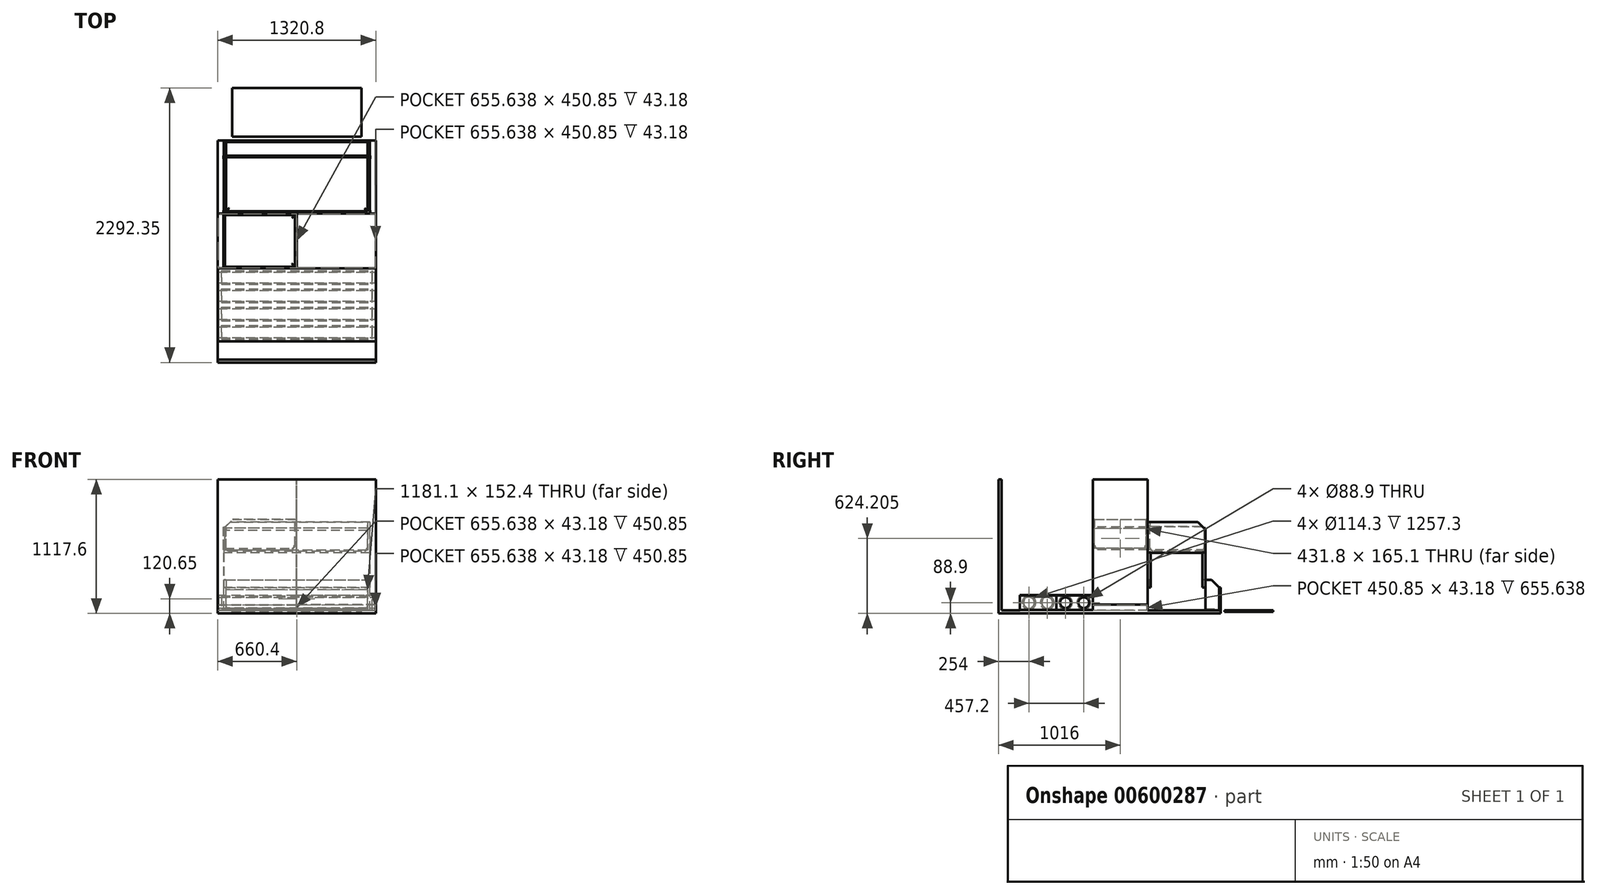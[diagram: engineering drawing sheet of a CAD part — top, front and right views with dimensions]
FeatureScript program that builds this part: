
annotation { "Feature Type Name" : "Feature", "Feature Type Description" : "" }
export const myFeature = defineFeature(function(context is Context, id is Id, definition is map)
    precondition{}
    {
        {
            var Q0;
            Q0=qCreatedBy(makeId("Top.planeOp"),FACE);
            var sketch = newSketch(context, id + "F0", { "sketchPlane" : qUnion([Q0])});
            skLineSegment(sketch, "E0.bottom", {"start": v(660.4, 914.4) * mm, "end": v(-660.4, 914.4) * mm});
            skLineSegment(sketch, "E0.top", {"start": v(660.4, -914.4) * mm, "end": v(-660.4, -914.4) * mm});
            skLineSegment(sketch, "E0.left", {"start": v(660.4, 914.4) * mm, "end": v(660.4, -914.4) * mm});
            skLineSegment(sketch, "E0.right", {"start": v(-660.4, 914.4) * mm, "end": v(-660.4, -914.4) * mm});
            skPoint(sketch, "E0.middle", {"position": v(0, 0) * mm});
            skSolve(sketch);
        }
        {
            var Q0;
            Q0 = qSketchRegion(id + "F0", true);
            extrude(context, id + "F1", {"entities" : qUnion([Q0]), "oppositeDirection" : true, "depth" : 25.4 * mm, "offsetDistance" : 25.4 * mm});
        }
        {
            var Q0;
            Q0=makeQuery(id+"F1.opExtrude","SWEPT_FACE",FACE,{"disambiguationData":[OSD([sQuery(id+"F0.wireOp",EDGE,"E0.top")])]});
            var sketch = newSketch(context, id + "F2", { "sketchPlane" : qUnion([Q0])});
            skLineSegment(sketch, "E1.bottom", {"start": v(-660.4, -25.4) * mm, "end": v(660.4, -25.4) * mm});
            skLineSegment(sketch, "E1.top", {"start": v(-660.4, 1092.2) * mm, "end": v(660.4, 1092.2) * mm});
            skLineSegment(sketch, "E1.left", {"start": v(-660.4, -25.4) * mm, "end": v(-660.4, 1092.2) * mm});
            skLineSegment(sketch, "E1.right", {"start": v(660.4, -25.4) * mm, "end": v(660.4, 1092.2) * mm});
            skSolve(sketch);
        }
        {
            var Q0;
            Q0 = qSketchRegion(id + "F2", true);
            extrude(context, id + "F3", {"entities" : qUnion([Q0]), "operationType" : NewBodyOperationType.ADD, "depth" : 25.4 * mm, "offsetDistance" : 25.4 * mm});
        }
        {
            var Q0;
            Q0=makeQuery(id+"F1.opExtrude","CAP_FACE",FACE,{"disambiguationData":[OSD([sQuery(id+"F0.wireOp",EDGE,"E0.bottom"),sQuery(id+"F0.wireOp",EDGE,"E0.top"),sQuery(id+"F0.wireOp",EDGE,"E0.left"),sQuery(id+"F0.wireOp",EDGE,"E0.right")])],"isStart":true});
            var sketch = newSketch(context, id + "F4", { "sketchPlane" : qUnion([Q0])});
            skLineSegment(sketch, "E2.bottom", {"start": v(-609.6, 914.4) * mm, "end": v(609.6, 914.4) * mm});
            skLineSegment(sketch, "E2.top", {"start": v(-609.6, 304.8) * mm, "end": v(609.6, 304.8) * mm});
            skLineSegment(sketch, "E2.left", {"start": v(-609.6, 914.4) * mm, "end": v(-609.6, 304.8) * mm});
            skLineSegment(sketch, "E2.right", {"start": v(609.6, 914.4) * mm, "end": v(609.6, 304.8) * mm});
            skLineSegment(sketch, "E3", {"start": v(0, 914.4) * mm, "end": v(0, 798.92) * mm, "construction": true});
            skPoint(sketch, "E3.endSnap0", {"position": v(0, 914.4) * mm});
            skPoint(sketch, "E4.visualSharp", {"position": v(-609.6, 914.4) * mm});
            skLineSegment(sketch, "E4.filletArc", {"start": v(-609.6, 914.4) * mm, "end": v(-609.6, 914.4) * mm});
            skPoint(sketch, "E5.visualSharp", {"position": v(-609.6, 304.8) * mm});
            skLineSegment(sketch, "E5.filletArc", {"start": v(-609.6, 304.8) * mm, "end": v(-609.6, 304.8) * mm});
            skPoint(sketch, "E6.visualSharp", {"position": v(609.6, 304.8) * mm});
            skLineSegment(sketch, "E6.filletArc", {"start": v(609.6, 304.8) * mm, "end": v(609.6, 304.8) * mm});
            skPoint(sketch, "E7.visualSharp", {"position": v(609.6, 914.4) * mm});
            skLineSegment(sketch, "E7.filletArc", {"start": v(609.6, 914.4) * mm, "end": v(609.6, 914.4) * mm});
            skSolve(sketch);
        }
        {
            var Q0;
            Q0 = qSketchRegion(id + "F4", true);
            extrude(context, id + "F5", {"entities" : qUnion([Q0]), "depth" : 254 * mm, "offsetDistance" : 25.4 * mm});
        }
        {
            var Q0;
            Q0=makeQuery(id+"F5.opExtrude","CAP_FACE",FACE,{"disambiguationData":[OSD([sQuery(id+"F4.wireOp",EDGE,"E2.bottom"),sQuery(id+"F4.wireOp",EDGE,"E2.top"),sQuery(id+"F4.wireOp",EDGE,"E2.left"),sQuery(id+"F4.wireOp",EDGE,"E2.right"),sQuery(id+"F4.wireOp",EDGE,"E4.filletArc"),sQuery(id+"F4.wireOp",EDGE,"E5.filletArc"),sQuery(id+"F4.wireOp",EDGE,"E6.filletArc"),sQuery(id+"F4.wireOp",EDGE,"E7.filletArc")])],"isStart":false});
            var sketch = newSketch(context, id + "F6", { "sketchPlane" : qUnion([Q0])});
            skLineSegment(sketch, "E8.0", {"start": v(590.55, 330.2) * mm, "end": v(590.55, 889) * mm});
            skLineSegment(sketch, "E8.1", {"start": v(-584.2, 323.85) * mm, "end": v(584.2, 323.85) * mm});
            skLineSegment(sketch, "E8.2", {"start": v(-590.55, 889) * mm, "end": v(-590.55, 330.2) * mm});
            skLineSegment(sketch, "E8.3", {"start": v(584.2, 895.35) * mm, "end": v(-584.2, 895.35) * mm});
            skPoint(sketch, "E9.visualSharp", {"position": v(-590.55, 895.35) * mm});
            skArc(sketch, "E9.filletArc", {"start": v(-584.2, 895.35) * mm, "mid": v(-588.7, 893.5) * mm, "end": v(-590.55, 889) * mm});
            skPoint(sketch, "E10.visualSharp", {"position": v(-590.55, 323.85) * mm});
            skArc(sketch, "E10.filletArc", {"start": v(-590.55, 330.2) * mm, "mid": v(-588.7, 325.7) * mm, "end": v(-584.2, 323.85) * mm});
            skPoint(sketch, "E11.visualSharp", {"position": v(590.55, 323.85) * mm});
            skArc(sketch, "E11.filletArc", {"start": v(584.2, 323.85) * mm, "mid": v(588.7, 325.7) * mm, "end": v(590.55, 330.2) * mm});
            skPoint(sketch, "E12.visualSharp", {"position": v(590.55, 895.35) * mm});
            skArc(sketch, "E12.filletArc", {"start": v(590.55, 889) * mm, "mid": v(588.7, 893.5) * mm, "end": v(584.2, 895.35) * mm});
            skLineSegment(sketch, "E13.bottom", {"start": v(-6.35, 895.35) * mm, "end": v(6.35, 895.35) * mm});
            skLineSegment(sketch, "E13.top", {"start": v(-6.35, 323.85) * mm, "end": v(6.35, 323.85) * mm});
            skLineSegment(sketch, "E13.left", {"start": v(-6.35, 895.35) * mm, "end": v(-6.35, 323.85) * mm, "construction": true});
            skLineSegment(sketch, "E13.right", {"start": v(6.35, 895.35) * mm, "end": v(6.35, 323.85) * mm, "construction": true});
            skLineSegment(sketch, "E14", {"start": v(0, 895.35) * mm, "end": v(0, 323.85) * mm, "construction": true});
            skSolve(sketch);
        }
        {
            var Q0;
            Q0=makeQuery(id+"F6.imprint","IMPRINT",FACE,{"disambiguationData":[TD([[makeQuery(id+"F6.imprint","IMPRINT",EDGE,{"derivedFrom":sQuery(id+"F6.wireOp",EDGE,"E8.0")}),1.0]])]});
            var Q1;
            Q1=makeQuery(id+"F6.imprint","IMPRINT",FACE,{"disambiguationData":[TD([[makeQuery(id+"F6.imprint","IMPRINT",EDGE,{"derivedFrom":sQuery(id+"F6.wireOp",EDGE,"E8.2")}),1.0]])]});
            extrude(context, id + "F7", {"entities" : qUnion([Q0, Q1]), "operationType" : NewBodyOperationType.REMOVE, "oppositeDirection" : true, "depth" : 241.3 * mm, "offsetDistance" : 25.4 * mm});
        }
        {
            var Q0;
            Q0=makeQuery(id+"F7.boolean.opBoolean","COPY",FACE,{"derivedFrom":makeQuery(id+"F7.opExtrude","CAP_FACE",FACE,{"disambiguationData":[OSD([sQuery(id+"F6.wireOp",EDGE,"E8.0"),sQuery(id+"F6.wireOp",EDGE,"E8.1"),sQuery(id+"F6.wireOp",EDGE,"E8.3"),sQuery(id+"F6.wireOp",EDGE,"E11.filletArc"),sQuery(id+"F6.wireOp",EDGE,"E12.filletArc"),sQuery(id+"F6.wireOp",EDGE,"E13.right")])],"isStart":false})});
            var Q1;
            Q1=makeQuery(id+"F7.boolean.opBoolean","COPY",FACE,{"derivedFrom":makeQuery(id+"F7.opExtrude","CAP_FACE",FACE,{"disambiguationData":[OSD([sQuery(id+"F6.wireOp",EDGE,"E8.1"),sQuery(id+"F6.wireOp",EDGE,"E8.2"),sQuery(id+"F6.wireOp",EDGE,"E8.3"),sQuery(id+"F6.wireOp",EDGE,"E9.filletArc"),sQuery(id+"F6.wireOp",EDGE,"E10.filletArc"),sQuery(id+"F6.wireOp",EDGE,"E13.left")])],"isStart":false})});
            fillet(context, id + "F8", {"entities" : qUnion([Q0, Q1]), "radius" : 25.4 * mm, "tangentPropagation" : true, "allowEdgeOverflow" : false});
        }
        {
            var Q0;
            Q0=makeQuery(id+"F1.opExtrude","SWEPT_FACE",FACE,{"disambiguationData":[OSD([sQuery(id+"F0.wireOp",EDGE,"E0.bottom")])]});
            cPlane(context, id + "F9", {"entities" : qUnion([Q0]), "cplaneType" : CPlaneType.OFFSET, "offset" : 127 * mm, "oppositeDirection" : true, "width" : 152.4 * mm, "height" : 152.4 * mm});
        }
        {
            var Q0;
            Q0=qCreatedBy(id+"F9.planeOp",FACE);
            var sketch = newSketch(context, id + "F10", { "sketchPlane" : qUnion([Q0])});
            skLineSegment(sketch, "E15.0", {"start": v(-660.4, 0) * mm, "end": v(660.4, 0) * mm});
            skLineSegment(sketch, "E16.bottom", {"start": v(-612.78, 0) * mm, "end": v(-609.6, 0) * mm});
            skLineSegment(sketch, "E16.top", {"start": v(-612.77, 482.6) * mm, "end": v(-609.6, 482.6) * mm});
            skLineSegment(sketch, "E16.left", {"start": v(-612.78, 0) * mm, "end": v(-612.77, 482.6) * mm});
            skLineSegment(sketch, "E16.right", {"start": v(-609.6, 0) * mm, "end": v(-609.6, 482.6) * mm});
            skLineSegment(sketch, "E17.bottom", {"start": v(-612.77, 482.6) * mm, "end": v(612.77, 482.6) * mm});
            skLineSegment(sketch, "E17.top", {"start": v(-612.77, 479.43) * mm, "end": v(612.77, 479.43) * mm});
            skLineSegment(sketch, "E17.left", {"start": v(-612.77, 482.6) * mm, "end": v(-612.77, 479.43) * mm});
            skLineSegment(sketch, "E17.right", {"start": v(612.78, 482.6) * mm, "end": v(612.78, 479.43) * mm});
            skLineSegment(sketch, "E18.bottom", {"start": v(612.77, 482.6) * mm, "end": v(609.6, 482.6) * mm});
            skLineSegment(sketch, "E18.top", {"start": v(612.78, 0) * mm, "end": v(609.6, 0) * mm});
            skLineSegment(sketch, "E18.left", {"start": v(612.78, 482.6) * mm, "end": v(612.77, 0) * mm});
            skLineSegment(sketch, "E18.right", {"start": v(609.6, 482.6) * mm, "end": v(609.6, 0) * mm});
            skLineSegment(sketch, "E19", {"start": v(0, 0) * mm, "end": v(0, 100.43) * mm, "construction": true});
            skLineSegment(sketch, "E20.bottom", {"start": v(-612.78, 0) * mm, "end": v(-600.08, 0) * mm});
            skLineSegment(sketch, "E20.top", {"start": v(-612.78, 3.18) * mm, "end": v(-600.08, 3.18) * mm});
            skLineSegment(sketch, "E20.left", {"start": v(-612.78, 0) * mm, "end": v(-612.78, 3.18) * mm});
            skLineSegment(sketch, "E20.right", {"start": v(-600.08, 0) * mm, "end": v(-600.08, 3.18) * mm});
            skLineSegment(sketch, "E21.MirrorCS", {"start": v(612.78, 3.18) * mm, "end": v(600.08, 3.18) * mm});
            skLineSegment(sketch, "E22.MirrorCS", {"start": v(600.08, 0) * mm, "end": v(600.08, 3.18) * mm});
            skSolve(sketch);
        }
        {
            var Q0;
            {var subQ0=sQuery(id+"F10.wireOp",EDGE,"E16.bottom");Q0=makeQuery(id+"F10.imprint","IMPRINT",FACE,{"disambiguationData":[TD([[makeQuery(id+"F10.imprint","IMPRINT",EDGE,{"derivedFrom":subQ0}),1.0]])]});}
            var Q1;
            {var subQ5=sQuery(id+"F10.wireOp",EDGE,"E17.left");Q1=makeQuery(id+"F10.imprint","IMPRINT",FACE,{"disambiguationData":[TD([[makeQuery(id+"F10.imprint","IMPRINT",EDGE,{"derivedFrom":subQ5}),1.0]])]});}
            var Q2;
            {var subQ5=sQuery(id+"F10.wireOp",EDGE,"E18.bottom");Q2=makeQuery(id+"F10.imprint","IMPRINT",FACE,{"disambiguationData":[TD([[makeQuery(id+"F10.imprint","IMPRINT",EDGE,{"derivedFrom":subQ5}),1.0]])]});}
            var Q3;
            {var subQ5=sQuery(id+"F10.wireOp",EDGE,"E18.top");Q3=makeQuery(id+"F10.imprint","IMPRINT",FACE,{"disambiguationData":[TD([[makeQuery(id+"F10.imprint","IMPRINT",EDGE,{"derivedFrom":subQ5}),-1.0]])]});}
            var Q4;
            {var subQ0=sQuery(id+"F10.wireOp",EDGE,"E17.bottom");var subQ1=sQuery(id+"F10.wireOp",EDGE,"E16.right");var subQ2=makeQuery(id+"F10.imprint","INTERSECT",VERTEX,{"derivedFrom":[subQ1,subQ0]});Q4=makeQuery(id+"F10.imprint","IMPRINT",FACE,{"disambiguationData":[TD([[makeQuery(id+"F10.imprint","IMPRINT",EDGE,{"disambiguationData":[TD([[subQ2,1.0]])],"derivedFrom":subQ1}),-1.0]])]});}
            var Q5;
            {var subQ3=sQuery(id+"F10.wireOp",EDGE,"E22.MirrorCS");Q5=makeQuery(id+"F10.imprint","IMPRINT",FACE,{"disambiguationData":[TD([[makeQuery(id+"F10.imprint","IMPRINT",EDGE,{"derivedFrom":subQ3}),-1.0]])]});}
            var Q6;
            {var subQ0=sQuery(id+"F10.wireOp",EDGE,"E18.left");var subQ1=sQuery(id+"F10.wireOp",EDGE,"E17.top");var subQ2=makeQuery(id+"F10.imprint","INTERSECT",VERTEX,{"derivedFrom":[subQ1,subQ0]});Q6=makeQuery(id+"F10.imprint","IMPRINT",FACE,{"disambiguationData":[TD([[makeQuery(id+"F10.imprint","IMPRINT",EDGE,{"disambiguationData":[TD([[subQ2,1.0]])],"derivedFrom":subQ1}),-1.0]])]});}
            var Q7;
            {var subQ5=sQuery(id+"F10.wireOp",EDGE,"E20.right");Q7=makeQuery(id+"F10.imprint","IMPRINT",FACE,{"disambiguationData":[TD([[makeQuery(id+"F10.imprint","IMPRINT",EDGE,{"derivedFrom":subQ5}),1.0]])]});}
            var Q8;
            {var subQ5=sQuery(id+"F10.wireOp",EDGE,"E20.left");Q8=makeQuery(id+"F10.imprint","IMPRINT",FACE,{"disambiguationData":[TD([[makeQuery(id+"F10.imprint","IMPRINT",EDGE,{"derivedFrom":subQ5}),-1.0]])]});}
            var Q9;
            {var subQ0=sQuery(id+"F10.wireOp",EDGE,"E16.left");Q9=makeQuery(id+"F10.imprint","IMPRINT",FACE,{"disambiguationData":[TD([[makeQuery(id+"F10.imprint","IMPRINT",EDGE,{"derivedFrom":subQ0}),-1.0]])]});}
            extrude(context, id + "F11", {"entities" : qUnion([Q0, Q1, Q2, Q3, Q4, Q5, Q6, Q7, Q8, Q9]), "oppositeDirection" : true, "depth" : 482.6 * mm, "offsetDistance" : 25.4 * mm});
        }
        {
            var Q0;
            Q0=makeQuery(id+"F5.opExtrude","SWEPT_FACE",FACE,{"disambiguationData":[OSD([sQuery(id+"F4.wireOp",EDGE,"E2.right")])]});
            var sketch = newSketch(context, id + "F12", { "sketchPlane" : qUnion([Q0])});
            skLineSegment(sketch, "E23", {"start": v(838.2, 254) * mm, "end": v(914.4, 177.8) * mm});
            skLineSegment(sketch, "E24.0", {"start": v(914.4, 254) * mm, "end": v(914.4, 0) * mm, "construction": true});
            skLineSegment(sketch, "E25.bottom", {"start": v(901.7, 0) * mm, "end": v(980.54, 0) * mm});
            skLineSegment(sketch, "E25.top", {"start": v(901.7, 254) * mm, "end": v(980.54, 254) * mm});
            skLineSegment(sketch, "E25.left", {"start": v(901.7, 0) * mm, "end": v(901.7, 190.5) * mm});
            skLineSegment(sketch, "E25.right", {"start": v(980.54, 0) * mm, "end": v(980.54, 254) * mm});
            skSolve(sketch);
        }
        {
            var Q0;
            Q0 = qSketchRegion(id + "F12", true);
            var Q1;
            {var subQ0=sQuery(id+"F12.wireOp",EDGE,"E23");var subQ1=sQuery(id+"F4.wireOp",EDGE,"E2.right");var subQ2=makeQuery(id+"F5.opExtrude","CAP_EDGE",EDGE,{"disambiguationData":[OSD([subQ1])],"isStart":false});var subQ3=makeQuery(id+"F12.imprint","INTERSECT",VERTEX,{"derivedFrom":[subQ2,subQ0]});Q1=makeQuery(id+"F12.imprint","IMPRINT",FACE,{"disambiguationData":[TD([[makeQuery(id+"F12.imprint","IMPRINT",EDGE,{"disambiguationData":[TD([[subQ3,-1.0]])],"derivedFrom":subQ0}),1.0]])]});}
            var Q2;
            {var subQ0=sQuery(id+"F12.wireOp",EDGE,"E25.left");Q2=makeQuery(id+"F12.imprint","IMPRINT",FACE,{"disambiguationData":[TD([[makeQuery(id+"F12.imprint","IMPRINT",EDGE,{"derivedFrom":subQ0}),-1.0]])]});}
            var Q3;
            {var subQ0=sQuery(id+"F12.wireOp",EDGE,"E25.right");Q3=makeQuery(id+"F12.imprint","IMPRINT",FACE,{"disambiguationData":[TD([[makeQuery(id+"F12.imprint","IMPRINT",EDGE,{"derivedFrom":subQ0}),1.0]])]});}
            extrude(context, id + "F13", {"entities" : qUnion([Q0, Q1, Q2, Q3]), "operationType" : NewBodyOperationType.REMOVE, "endBound" : BoundingType.THROUGH_ALL, "oppositeDirection" : true, "depth" : 25.4 * mm, "offsetDistance" : 25.4 * mm});
        }
        {
            var Q0;
            Q0=makeQuery(id+"F13.boolean.opBoolean","COPY",FACE,{"derivedFrom":makeQuery(id+"F13.opExtrude","SWEPT_FACE",FACE,{"disambiguationData":[OSD([sQuery(id+"F12.wireOp",EDGE,"E25.left")])]})});
            var sketch = newSketch(context, id + "F14", { "sketchPlane" : qUnion([Q0])});
            skArc(sketch, "E26.0.0", {"start": v(-565.15, 12.7) * mm, "mid": v(-583.11, 20.14) * mm, "end": v(-590.55, 38.1) * mm});
            skArc(sketch, "E26.0.2", {"start": v(-590.55, 38.1) * mm, "mid": v(-583.11, 20.14) * mm, "end": v(-565.15, 12.7) * mm});
            skLineSegment(sketch, "E27.0.0", {"start": v(565.15, 12.7) * mm, "end": v(-565.15, 12.7) * mm});
            skLineSegment(sketch, "E27.0.2", {"start": v(-565.15, 12.7) * mm, "end": v(565.15, 12.7) * mm});
            skArc(sketch, "E28.0.0", {"start": v(590.55, 38.1) * mm, "mid": v(583.11, 20.14) * mm, "end": v(565.15, 12.7) * mm});
            skArc(sketch, "E28.0.2", {"start": v(590.55, 38.1) * mm, "mid": v(583.11, 20.14) * mm, "end": v(565.15, 12.7) * mm});
            skLineSegment(sketch, "E29.0", {"start": v(-590.55, 38.1) * mm, "end": v(-590.55, 203.2) * mm});
            skLineSegment(sketch, "E30.0", {"start": v(590.55, 38.1) * mm, "end": v(590.55, 203.2) * mm});
            skLineSegment(sketch, "E31", {"start": v(590.55, 203.2) * mm, "end": v(-590.55, 203.2) * mm});
            skSolve(sketch);
        }
        {
            var Q0;
            Q0 = qSketchRegion(id + "F14", true);
            extrude(context, id + "F15", {"entities" : qUnion([Q0]), "operationType" : NewBodyOperationType.REMOVE, "oppositeDirection" : true, "depth" : 50.8 * mm, "offsetDistance" : 25.4 * mm});
        }
        {
            var Q0;
            Q0=makeQuery(id+"F13.boolean.opBoolean","COPY",FACE,{"derivedFrom":makeQuery(id+"F13.opExtrude","SWEPT_FACE",FACE,{"disambiguationData":[OSD([sQuery(id+"F12.wireOp",EDGE,"E25.left")])]})});
            var sketch = newSketch(context, id + "F16", { "sketchPlane" : qUnion([Q0])});
            skLineSegment(sketch, "E32.bottom", {"start": v(-609.6, 190.5) * mm, "end": v(609.6, 190.5) * mm});
            skLineSegment(sketch, "E32.top", {"start": v(-609.6, 0) * mm, "end": v(609.6, 0) * mm});
            skLineSegment(sketch, "E32.left", {"start": v(-609.6, 190.5) * mm, "end": v(-609.6, 0) * mm});
            skLineSegment(sketch, "E32.right", {"start": v(609.6, 190.5) * mm, "end": v(609.6, 0) * mm});
            skLineSegment(sketch, "E33.0", {"start": v(-590.55, 171.45) * mm, "end": v(590.55, 171.45) * mm});
            skLineSegment(sketch, "E33.1", {"start": v(-590.55, 171.45) * mm, "end": v(-590.55, 19.05) * mm});
            skLineSegment(sketch, "E33.2", {"start": v(-590.55, 19.05) * mm, "end": v(590.55, 19.05) * mm});
            skLineSegment(sketch, "E33.3", {"start": v(590.55, 171.45) * mm, "end": v(590.55, 19.05) * mm});
            skSolve(sketch);
        }
        {
            var Q0;
            Q0 = qSketchRegion(id + "F16", true);
            extrude(context, id + "F17", {"entities" : qUnion([Q0]), "depth" : 12.7 * mm, "offsetDistance" : 25.4 * mm});
        }
        {
            var Q0;
            Q0=makeQuery(id+"F17.opExtrude","CAP_FACE",FACE,{"disambiguationData":[OSD([sQuery(id+"F16.wireOp",EDGE,"E32.bottom"),sQuery(id+"F16.wireOp",EDGE,"E32.top"),sQuery(id+"F16.wireOp",EDGE,"E32.left"),sQuery(id+"F16.wireOp",EDGE,"E32.right"),sQuery(id+"F16.wireOp",EDGE,"E33.0"),sQuery(id+"F16.wireOp",EDGE,"E33.1"),sQuery(id+"F16.wireOp",EDGE,"E33.2"),sQuery(id+"F16.wireOp",EDGE,"E33.3")])],"isStart":false});
            var sketch = newSketch(context, id + "F18", { "sketchPlane" : qUnion([Q0])});
            skLineSegment(sketch, "E34.0", {"start": v(-590.55, 171.45) * mm, "end": v(590.55, 171.45) * mm});
            skLineSegment(sketch, "E34.1", {"start": v(-590.55, 171.45) * mm, "end": v(-590.55, 19.05) * mm});
            skLineSegment(sketch, "E34.2", {"start": v(-590.55, 19.05) * mm, "end": v(590.55, 19.05) * mm});
            skLineSegment(sketch, "E34.3", {"start": v(590.55, 19.05) * mm, "end": v(590.55, 171.45) * mm});
            skSolve(sketch);
        }
        {
            var Q0;
            Q0 = qSketchRegion(id + "F18", true);
            extrude(context, id + "F19", {"entities" : qUnion([Q0]), "oppositeDirection" : true, "depth" : 12.7 * mm, "offsetDistance" : 25.4 * mm});
        }
        {
            var Q0;
            Q0=makeQuery(id+"F11.opExtrude","SWEPT_FACE",FACE,{"disambiguationData":[OSD([sQuery(id+"F10.wireOp",EDGE,"E17.bottom"),sQuery(id+"F10.wireOp",EDGE,"E18.bottom")])]});
            var sketch = newSketch(context, id + "F20", { "sketchPlane" : qUnion([Q0])});
            skLineSegment(sketch, "E35.bottom", {"start": v(-609.6, 304.8) * mm, "end": v(609.6, 304.8) * mm});
            skLineSegment(sketch, "E35.top", {"start": v(-609.6, 787.4) * mm, "end": v(609.6, 787.4) * mm});
            skLineSegment(sketch, "E35.left", {"start": v(-609.6, 304.8) * mm, "end": v(-609.6, 787.4) * mm});
            skLineSegment(sketch, "E35.right", {"start": v(609.6, 304.8) * mm, "end": v(609.6, 787.4) * mm});
            skLineSegment(sketch, "E36", {"start": v(0, 0) * mm, "end": v(0, 135.1) * mm, "construction": true});
            skSolve(sketch);
        }
        {
            var Q0;
            Q0 = qSketchRegion(id + "F20", true);
            extrude(context, id + "F21", {"entities" : qUnion([Q0]), "depth" : 254 * mm, "offsetDistance" : 25.4 * mm});
        }
        {
            var Q0;
            Q0=makeQuery(id+"F21.opExtrude","CAP_FACE",FACE,{"disambiguationData":[OSD([sQuery(id+"F20.wireOp",EDGE,"E35.bottom"),sQuery(id+"F20.wireOp",EDGE,"E35.top"),sQuery(id+"F20.wireOp",EDGE,"E35.left"),sQuery(id+"F20.wireOp",EDGE,"E35.right")])],"isStart":false});
            var sketch = newSketch(context, id + "F22", { "sketchPlane" : qUnion([Q0])});
            skLineSegment(sketch, "E37.0", {"start": v(-584.2, 323.85) * mm, "end": v(584.2, 323.85) * mm});
            skLineSegment(sketch, "E37.1", {"start": v(-590.55, 762) * mm, "end": v(-590.55, 330.2) * mm});
            skLineSegment(sketch, "E37.2", {"start": v(584.2, 768.35) * mm, "end": v(-584.2, 768.35) * mm});
            skLineSegment(sketch, "E37.3", {"start": v(590.55, 330.2) * mm, "end": v(590.55, 762) * mm});
            skPoint(sketch, "E38.visualSharp", {"position": v(-590.55, 768.35) * mm});
            skArc(sketch, "E38.filletArc", {"start": v(-584.2, 768.35) * mm, "mid": v(-588.7, 766.5) * mm, "end": v(-590.55, 762) * mm});
            skPoint(sketch, "E39.visualSharp", {"position": v(-590.55, 323.85) * mm});
            skArc(sketch, "E39.filletArc", {"start": v(-590.55, 330.2) * mm, "mid": v(-588.7, 325.7) * mm, "end": v(-584.2, 323.85) * mm});
            skPoint(sketch, "E40.visualSharp", {"position": v(590.55, 323.85) * mm});
            skArc(sketch, "E40.filletArc", {"start": v(584.2, 323.85) * mm, "mid": v(588.7, 325.7) * mm, "end": v(590.55, 330.2) * mm});
            skPoint(sketch, "E41.visualSharp", {"position": v(590.55, 768.35) * mm});
            skArc(sketch, "E41.filletArc", {"start": v(590.55, 762) * mm, "mid": v(588.7, 766.5) * mm, "end": v(584.2, 768.35) * mm});
            skSolve(sketch);
        }
        {
            var Q0;
            Q0 = qSketchRegion(id + "F22", true);
            extrude(context, id + "F23", {"entities" : qUnion([Q0]), "operationType" : NewBodyOperationType.REMOVE, "oppositeDirection" : true, "depth" : 241.3 * mm, "offsetDistance" : 25.4 * mm});
        }
        {
            var Q0;
            Q0=makeQuery(id+"F23.boolean.opBoolean","COPY",EDGE,{"derivedFrom":makeQuery(id+"F23.opExtrude","CAP_EDGE",EDGE,{"disambiguationData":[OSD([sQuery(id+"F22.wireOp",EDGE,"E37.0")])],"isStart":false})});
            var Q1;
            Q1=makeQuery(id+"F23.boolean.opBoolean","COPY",EDGE,{"derivedFrom":makeQuery(id+"F23.opExtrude","CAP_EDGE",EDGE,{"disambiguationData":[OSD([sQuery(id+"F22.wireOp",EDGE,"E37.1")])],"isStart":false})});
            var Q2;
            Q2=makeQuery(id+"F23.boolean.opBoolean","COPY",EDGE,{"derivedFrom":makeQuery(id+"F23.opExtrude","CAP_EDGE",EDGE,{"disambiguationData":[OSD([sQuery(id+"F22.wireOp",EDGE,"E37.3")])],"isStart":false})});
            fillet(context, id + "F24", {"entities" : qUnion([Q0, Q1, Q2]), "radius" : 25.4 * mm, "tangentPropagation" : true, "allowEdgeOverflow" : false});
        }
        {
            var Q0;
            Q0=makeQuery(id+"F21.opExtrude","SWEPT_FACE",FACE,{"disambiguationData":[OSD([sQuery(id+"F20.wireOp",EDGE,"E35.right")])]});
            var sketch = newSketch(context, id + "F25", { "sketchPlane" : qUnion([Q0])});
            skLineSegment(sketch, "E42", {"start": v(723.9, 736.6) * mm, "end": v(774.7, 685.8) * mm});
            skLineSegment(sketch, "E43.bottom", {"start": v(787.4, 482.6) * mm, "end": v(774.7, 482.6) * mm});
            skLineSegment(sketch, "E43.top", {"start": v(787.4, 736.6) * mm, "end": v(774.7, 736.6) * mm});
            skLineSegment(sketch, "E43.left", {"start": v(787.4, 482.6) * mm, "end": v(787.4, 736.6) * mm});
            skLineSegment(sketch, "E43.right", {"start": v(774.7, 482.6) * mm, "end": v(774.7, 685.8) * mm});
            skLineSegment(sketch, "E44", {"start": v(723.9, 736.6) * mm, "end": v(787.4, 736.6) * mm});
            skPoint(sketch, "E45.orphan", {"position": v(787.4, 673.1) * mm});
            skSolve(sketch);
        }
        {
            var Q0;
            Q0 = qSketchRegion(id + "F25", true);
            extrude(context, id + "F26", {"entities" : qUnion([Q0]), "operationType" : NewBodyOperationType.REMOVE, "endBound" : BoundingType.THROUGH_ALL, "oppositeDirection" : true, "depth" : 25.4 * mm, "offsetDistance" : 25.4 * mm});
        }
        {
            var Q0;
            Q0=makeQuery(id+"F26.boolean.opBoolean","COPY",FACE,{"derivedFrom":makeQuery(id+"F26.opExtrude","SWEPT_FACE",FACE,{"disambiguationData":[OSD([sQuery(id+"F25.wireOp",EDGE,"E43.right")])]})});
            var sketch = newSketch(context, id + "F27", { "sketchPlane" : qUnion([Q0])});
            skArc(sketch, "E46.0.0", {"start": v(-565.15, 495.3) * mm, "mid": v(-583.11, 502.74) * mm, "end": v(-590.55, 520.7) * mm});
            skArc(sketch, "E46.0.2", {"start": v(-590.55, 520.7) * mm, "mid": v(-583.11, 502.74) * mm, "end": v(-565.15, 495.3) * mm});
            skLineSegment(sketch, "E47.0", {"start": v(-590.55, 520.7) * mm, "end": v(-590.55, 698.5) * mm});
            skLineSegment(sketch, "E48.0", {"start": v(-565.15, 495.3) * mm, "end": v(565.15, 495.3) * mm});
            skArc(sketch, "E49.0.0", {"start": v(590.55, 520.7) * mm, "mid": v(583.11, 502.74) * mm, "end": v(565.15, 495.3) * mm});
            skArc(sketch, "E49.0.2", {"start": v(590.55, 520.7) * mm, "mid": v(583.11, 502.74) * mm, "end": v(565.15, 495.3) * mm});
            skLineSegment(sketch, "E50.0", {"start": v(590.55, 520.7) * mm, "end": v(590.55, 698.5) * mm});
            skLineSegment(sketch, "E51", {"start": v(590.55, 698.5) * mm, "end": v(-590.55, 698.5) * mm});
            skSolve(sketch);
        }
        {
            var Q0;
            Q0 = qSketchRegion(id + "F27", true);
            extrude(context, id + "F28", {"entities" : qUnion([Q0]), "operationType" : NewBodyOperationType.REMOVE, "oppositeDirection" : true, "depth" : 50.8 * mm, "offsetDistance" : 25.4 * mm});
        }
        {
            var Q0;
            Q0=makeQuery(id+"F26.boolean.opBoolean","COPY",FACE,{"derivedFrom":makeQuery(id+"F26.opExtrude","SWEPT_FACE",FACE,{"disambiguationData":[OSD([sQuery(id+"F25.wireOp",EDGE,"E43.right")])]})});
            var sketch = newSketch(context, id + "F29", { "sketchPlane" : qUnion([Q0])});
            skLineSegment(sketch, "E52.bottom", {"start": v(-609.6, 685.8) * mm, "end": v(609.6, 685.8) * mm});
            skLineSegment(sketch, "E52.top", {"start": v(-609.6, 482.6) * mm, "end": v(609.6, 482.6) * mm});
            skLineSegment(sketch, "E52.left", {"start": v(-609.6, 685.8) * mm, "end": v(-609.6, 482.6) * mm});
            skLineSegment(sketch, "E52.right", {"start": v(609.6, 685.8) * mm, "end": v(609.6, 482.6) * mm});
            skLineSegment(sketch, "E53.0", {"start": v(-590.55, 666.75) * mm, "end": v(590.55, 666.75) * mm});
            skLineSegment(sketch, "E53.1", {"start": v(-590.55, 666.75) * mm, "end": v(-590.55, 501.65) * mm});
            skLineSegment(sketch, "E53.2", {"start": v(-590.55, 501.65) * mm, "end": v(590.55, 501.65) * mm});
            skLineSegment(sketch, "E53.3", {"start": v(590.55, 666.75) * mm, "end": v(590.55, 501.65) * mm});
            skSolve(sketch);
        }
        {
            var Q0;
            Q0 = qSketchRegion(id + "F29", true);
            extrude(context, id + "F30", {"entities" : qUnion([Q0]), "depth" : 12.7 * mm, "offsetDistance" : 25.4 * mm});
        }
        {
            var Q0;
            Q0=makeQuery(id+"F30.opExtrude","CAP_FACE",FACE,{"disambiguationData":[OSD([sQuery(id+"F29.wireOp",EDGE,"E52.bottom"),sQuery(id+"F29.wireOp",EDGE,"E52.top"),sQuery(id+"F29.wireOp",EDGE,"E52.left"),sQuery(id+"F29.wireOp",EDGE,"E52.right"),sQuery(id+"F29.wireOp",EDGE,"E53.0"),sQuery(id+"F29.wireOp",EDGE,"E53.1"),sQuery(id+"F29.wireOp",EDGE,"E53.2"),sQuery(id+"F29.wireOp",EDGE,"E53.3")])],"isStart":false});
            var sketch = newSketch(context, id + "F31", { "sketchPlane" : qUnion([Q0])});
            skLineSegment(sketch, "E54.0", {"start": v(-590.55, 666.75) * mm, "end": v(-590.55, 501.65) * mm});
            skLineSegment(sketch, "E54.1", {"start": v(-590.55, 666.75) * mm, "end": v(590.55, 666.75) * mm});
            skLineSegment(sketch, "E54.2", {"start": v(-590.55, 501.65) * mm, "end": v(590.55, 501.65) * mm});
            skLineSegment(sketch, "E54.3", {"start": v(590.55, 666.75) * mm, "end": v(590.55, 501.65) * mm});
            skSolve(sketch);
        }
        {
            var Q0;
            Q0 = qSketchRegion(id + "F31", true);
            extrude(context, id + "F32", {"entities" : qUnion([Q0]), "oppositeDirection" : true, "depth" : 12.7 * mm, "offsetDistance" : 25.4 * mm});
        }
        {
            var Q0;
            Q0=makeQuery(id+"F11.opExtrude","SWEPT_FACE",FACE,{"disambiguationData":[OSD([sQuery(id+"F10.wireOp",EDGE,"E18.left")])]});
            var sketch = newSketch(context, id + "F33", { "sketchPlane" : qUnion([Q0])});
            skLineSegment(sketch, "E55.bottom", {"start": v(-762, 482.6) * mm, "end": v(-330.2, 482.6) * mm});
            skLineSegment(sketch, "E55.top", {"start": v(-762, 190.5) * mm, "end": v(-330.2, 190.5) * mm});
            skLineSegment(sketch, "E55.left", {"start": v(-762, 482.6) * mm, "end": v(-762, 190.5) * mm});
            skLineSegment(sketch, "E55.right", {"start": v(-330.2, 482.6) * mm, "end": v(-330.2, 190.5) * mm});
            skLineSegment(sketch, "E56.bottom", {"start": v(-787.4, 190.5) * mm, "end": v(-304.8, 190.5) * mm});
            skLineSegment(sketch, "E56.top", {"start": v(-787.4, 0) * mm, "end": v(-304.8, 0) * mm});
            skLineSegment(sketch, "E56.left", {"start": v(-787.4, 190.5) * mm, "end": v(-787.4, 0) * mm});
            skLineSegment(sketch, "E56.right", {"start": v(-304.8, 190.5) * mm, "end": v(-304.8, 0) * mm});
            skLineSegment(sketch, "E57", {"start": v(-546.1, 482.6) * mm, "end": v(-546.1, 321.82) * mm, "construction": true});
            skPoint(sketch, "E57.endSnap0", {"position": v(-546.1, 482.6) * mm});
            skSolve(sketch);
        }
        {
            var Q0;
            Q0=makeQuery(id+"F3.boolean.opBoolean","MERGE",FACE,{"derivedFrom":[makeQuery(id+"F1.opExtrude","SWEPT_FACE",FACE,{"disambiguationData":[OSD([sQuery(id+"F0.wireOp",EDGE,"E0.left")])]}),makeQuery(id+"F3.opExtrude","SWEPT_FACE",FACE,{"disambiguationData":[OSD([sQuery(id+"F2.wireOp",EDGE,"E1.right")])]})]});
            cPlane(context, id + "F34", {"entities" : qUnion([Q0]), "cplaneType" : CPlaneType.OFFSET, "offset" : 6.35 * mm, "oppositeDirection" : true, "width" : 152.4 * mm, "height" : 152.4 * mm});
        }
        {
            var Q0;
            Q0 = qSketchRegion(id + "F33", true);
            extrude(context, id + "F35", {"entities" : qUnion([Q0]), "operationType" : NewBodyOperationType.REMOVE, "endBound" : BoundingType.THROUGH_ALL, "oppositeDirection" : true, "depth" : 3.17 * mm, "offsetDistance" : 25.4 * mm});
        }
        {
            var Q0;
            Q0=qCreatedBy(id+"F34.planeOp",FACE);
            var sketch = newSketch(context, id + "F36", { "sketchPlane" : qUnion([Q0])});
            skLineSegment(sketch, "E58.bottom", {"start": v(-152.4, 0) * mm, "end": v(-762, 0) * mm});
            skLineSegment(sketch, "E58.top", {"start": v(-152.4, 127) * mm, "end": v(-762, 127) * mm});
            skLineSegment(sketch, "E58.left", {"start": v(-152.4, 0) * mm, "end": v(-152.4, 127) * mm});
            skLineSegment(sketch, "E58.right", {"start": v(-762, 0) * mm, "end": v(-762, 127) * mm});
            skSolve(sketch);
        }
        {
            var Q0;
            Q0 = qSketchRegion(id + "F36", true);
            extrude(context, id + "F37", {"entities" : qUnion([Q0]), "oppositeDirection" : true, "depth" : 1308.1 * mm, "offsetDistance" : 25.4 * mm});
        }
        {
            var Q0;
            Q0=makeQuery(id+"F37.opExtrude","CAP_FACE",FACE,{"disambiguationData":[OSD([sQuery(id+"F36.wireOp",EDGE,"E58.bottom"),sQuery(id+"F36.wireOp",EDGE,"E58.top"),sQuery(id+"F36.wireOp",EDGE,"E58.left"),sQuery(id+"F36.wireOp",EDGE,"E58.right")])],"isStart":true});
            var sketch = newSketch(context, id + "F38", { "sketchPlane" : qUnion([Q0])});
            skCircle(sketch, "E59", {"center": v(-685.8, 63.5) * mm, "radius": 57.15 * mm});
            skCircle(sketch, "E60", {"center": v(-533.4, 63.5) * mm, "radius": 57.15 * mm});
            skCircle(sketch, "E61", {"center": v(-228.6, 63.5) * mm, "radius": 57.15 * mm});
            skLineSegment(sketch, "E62", {"start": v(-457.2, 127) * mm, "end": v(-457.2, 123.13) * mm, "construction": true});
            skCircle(sketch, "E63", {"center": v(-381, 63.5) * mm, "radius": 57.15 * mm});
            skSolve(sketch);
        }
        {
            var Q0;
            Q0 = qSketchRegion(id + "F38", true);
            extrude(context, id + "F39", {"entities" : qUnion([Q0]), "operationType" : NewBodyOperationType.REMOVE, "endBound" : BoundingType.THROUGH_ALL, "oppositeDirection" : true, "depth" : 25.4 * mm, "offsetDistance" : 25.4 * mm});
        }
        {
            var Q0;
            Q0=makeQuery(id+"F37.opExtrude","CAP_FACE",FACE,{"disambiguationData":[OSD([sQuery(id+"F36.wireOp",EDGE,"E58.bottom"),sQuery(id+"F36.wireOp",EDGE,"E58.top"),sQuery(id+"F36.wireOp",EDGE,"E58.left"),sQuery(id+"F36.wireOp",EDGE,"E58.right")])],"isStart":true});
            var sketch = newSketch(context, id + "F40", { "sketchPlane" : qUnion([Q0])});
            skCircle(sketch, "E64.0", {"center": v(-685.8, 63.5) * mm, "radius": 57.15 * mm});
            skCircle(sketch, "E64.1", {"center": v(-533.4, 63.5) * mm, "radius": 57.15 * mm});
            skCircle(sketch, "E65.0", {"center": v(-381, 63.5) * mm, "radius": 57.15 * mm});
            skCircle(sketch, "E65.1", {"center": v(-228.6, 63.5) * mm, "radius": 57.15 * mm});
            skCircle(sketch, "E66", {"center": v(-685.8, 63.5) * mm, "radius": 44.45 * mm});
            skCircle(sketch, "E67", {"center": v(-533.4, 63.5) * mm, "radius": 44.45 * mm});
            skCircle(sketch, "E68", {"center": v(-381, 63.5) * mm, "radius": 44.45 * mm});
            skCircle(sketch, "E69", {"center": v(-228.6, 63.5) * mm, "radius": 44.45 * mm});
            skCircle(sketch, "E70", {"center": v(-228.6, 63.5) * mm, "radius": 47.62 * mm});
            skCircle(sketch, "E71", {"center": v(-381, 63.5) * mm, "radius": 47.62 * mm});
            skCircle(sketch, "E72", {"center": v(-533.4, 63.5) * mm, "radius": 47.62 * mm});
            skCircle(sketch, "E73", {"center": v(-685.8, 63.5) * mm, "radius": 47.62 * mm});
            skSolve(sketch);
        }
        {
            var Q0;
            Q0=makeQuery(id+"F40.imprint","IMPRINT",FACE,{"disambiguationData":[TD([[makeQuery(id+"F40.imprint","IMPRINT",EDGE,{"derivedFrom":sQuery(id+"F40.wireOp",EDGE,"E66")}),-1.0]])]});
            var Q1;
            Q1=makeQuery(id+"F40.imprint","IMPRINT",FACE,{"disambiguationData":[TD([[makeQuery(id+"F40.imprint","IMPRINT",EDGE,{"derivedFrom":sQuery(id+"F40.wireOp",EDGE,"E67")}),-1.0]])]});
            var Q2;
            Q2=makeQuery(id+"F40.imprint","IMPRINT",FACE,{"disambiguationData":[TD([[makeQuery(id+"F40.imprint","IMPRINT",EDGE,{"derivedFrom":sQuery(id+"F40.wireOp",EDGE,"E68")}),-1.0]])]});
            var Q3;
            Q3=makeQuery(id+"F40.imprint","IMPRINT",FACE,{"disambiguationData":[TD([[makeQuery(id+"F40.imprint","IMPRINT",EDGE,{"derivedFrom":sQuery(id+"F40.wireOp",EDGE,"E69")}),-1.0]])]});
            extrude(context, id + "F41", {"entities" : qUnion([Q0, Q1, Q2, Q3]), "oppositeDirection" : true, "depth" : 1308.1 * mm, "offsetDistance" : 25.4 * mm});
        }
        {
            var Q0;
            Q0 = qSketchRegion(id + "F40", true);
            extrude(context, id + "F42", {"entities" : qUnion([Q0]), "operationType" : NewBodyOperationType.ADD, "oppositeDirection" : true, "depth" : 25.4 * mm, "offsetDistance" : 25.4 * mm});
        }
        {
            var Q0;
            Q0=makeQuery(id+"F37.opExtrude","CAP_FACE",FACE,{"disambiguationData":[OSD([sQuery(id+"F36.wireOp",EDGE,"E58.bottom"),sQuery(id+"F36.wireOp",EDGE,"E58.top"),sQuery(id+"F36.wireOp",EDGE,"E58.left"),sQuery(id+"F36.wireOp",EDGE,"E58.right")])],"isStart":false});
            var sketch = newSketch(context, id + "F43", { "sketchPlane" : qUnion([Q0])});
            skCircle(sketch, "E74.0", {"center": v(685.8, 63.5) * mm, "radius": 47.62 * mm});
            skCircle(sketch, "E74.1", {"center": v(685.8, 63.5) * mm, "radius": 57.15 * mm});
            skCircle(sketch, "E74.2", {"center": v(533.4, 63.5) * mm, "radius": 47.62 * mm});
            skCircle(sketch, "E74.3", {"center": v(533.4, 63.5) * mm, "radius": 57.15 * mm});
            skCircle(sketch, "E74.4", {"center": v(381, 63.5) * mm, "radius": 47.62 * mm});
            skCircle(sketch, "E74.5", {"center": v(381, 63.5) * mm, "radius": 57.15 * mm});
            skCircle(sketch, "E74.6", {"center": v(228.6, 63.5) * mm, "radius": 57.15 * mm});
            skCircle(sketch, "E74.7", {"center": v(228.6, 63.5) * mm, "radius": 47.62 * mm});
            skSolve(sketch);
        }
        {
            var Q0;
            Q0 = qSketchRegion(id + "F43", true);
            extrude(context, id + "F44", {"entities" : qUnion([Q0]), "operationType" : NewBodyOperationType.ADD, "oppositeDirection" : true, "depth" : 25.4 * mm, "offsetDistance" : 25.4 * mm});
        }
        {
            var Q0;
            Q0=makeQuery(id+"F21.opExtrude","CAP_FACE",FACE,{"disambiguationData":[OSD([sQuery(id+"F20.wireOp",EDGE,"E35.bottom"),sQuery(id+"F20.wireOp",EDGE,"E35.top"),sQuery(id+"F20.wireOp",EDGE,"E35.left"),sQuery(id+"F20.wireOp",EDGE,"E35.right")])],"isStart":true});
            extrude(context, id + "F45", {"entities" : qUnion([Q0]), "operationType" : NewBodyOperationType.ADD, "depth" : 3.17 * mm, "offsetDistance" : 25.4 * mm});
        }
        {
            var Q0;
            Q0=qCreatedBy(makeId("Right.planeOp"),FACE);
            var sketch = newSketch(context, id + "F46", { "sketchPlane" : qUnion([Q0])});
            skLineSegment(sketch, "E75.0", {"start": v(914.4, 0) * mm, "end": v(-914.4, 0) * mm});
            skLineSegment(sketch, "E76.bottom", {"start": v(-152.4, 0) * mm, "end": v(304.8, 0) * mm});
            skLineSegment(sketch, "E76.top", {"start": v(-152.4, 1092.2) * mm, "end": v(304.8, 1092.2) * mm});
            skLineSegment(sketch, "E76.left", {"start": v(-152.4, 0) * mm, "end": v(-152.4, 1092.2) * mm});
            skLineSegment(sketch, "E76.right", {"start": v(304.8, 0) * mm, "end": v(304.8, 1092.2) * mm});
            skLineSegment(sketch, "E77.0", {"start": v(-152.4, 0) * mm, "end": v(-152.4, 127) * mm});
            skPoint(sketch, "E78.0", {"position": v(304.8, 0) * mm});
            skSolve(sketch);
        }
        {
            var Q0;
            Q0 = qSketchRegion(id + "F46", true);
            extrude(context, id + "F47", {"entities" : qUnion([Q0]), "depth" : 3.17 * mm, "offsetDistance" : 25.4 * mm, "symmetric" : true});
        }
        {
            var Q0;
            Q0=makeQuery(id+"F47.opExtrude","CAP_FACE",FACE,{"disambiguationData":[OSD([sQuery(id+"F46.wireOp",EDGE,"E76.bottom"),sQuery(id+"F46.wireOp",EDGE,"E76.top"),sQuery(id+"F46.wireOp",EDGE,"E76.left"),sQuery(id+"F46.wireOp",EDGE,"E76.right"),sQuery(id+"F46.wireOp",EDGE,"E77.0")])],"isStart":false});
            var sketch = newSketch(context, id + "F48", { "sketchPlane" : qUnion([Q0])});
            skLineSegment(sketch, "E79.bottom", {"start": v(-152.4, 20.96) * mm, "end": v(-149.22, 20.96) * mm});
            skLineSegment(sketch, "E79.top", {"start": v(-152.4, 46.36) * mm, "end": v(-149.22, 46.36) * mm});
            skLineSegment(sketch, "E79.left", {"start": v(-152.4, 20.96) * mm, "end": v(-152.4, 46.36) * mm});
            skLineSegment(sketch, "E79.right", {"start": v(-149.22, 20.96) * mm, "end": v(-149.22, 46.36) * mm});
            skLineSegment(sketch, "E80.bottom", {"start": v(-152.4, 46.36) * mm, "end": v(304.8, 46.36) * mm});
            skLineSegment(sketch, "E80.top", {"start": v(-152.4, 43.18) * mm, "end": v(304.8, 43.18) * mm});
            skLineSegment(sketch, "E80.left", {"start": v(-152.4, 46.36) * mm, "end": v(-152.4, 43.18) * mm});
            skLineSegment(sketch, "E80.right", {"start": v(304.8, 46.35) * mm, "end": v(304.8, 43.18) * mm});
            skLineSegment(sketch, "E81.top", {"start": v(-152.4, 0) * mm, "end": v(-149.22, 0) * mm});
            skLineSegment(sketch, "E81.left", {"start": v(-152.4, 20.96) * mm, "end": v(-152.4, 0) * mm});
            skLineSegment(sketch, "E81.right", {"start": v(-149.22, 20.96) * mm, "end": v(-149.22, 0) * mm});
            skSolve(sketch);
        }
        {
            var Q0;
            Q0 = qSketchRegion(id + "F48", true);
            extrude(context, id + "F49", {"entities" : qUnion([Q0]), "operationType" : NewBodyOperationType.ADD, "depth" : 658.8 * mm, "offsetDistance" : 25.4 * mm});
        }
        {
            var Q0;
            Q0=makeQuery(id+"F47.opExtrude","CAP_FACE",FACE,{"disambiguationData":[OSD([sQuery(id+"F46.wireOp",EDGE,"E76.bottom"),sQuery(id+"F46.wireOp",EDGE,"E76.top"),sQuery(id+"F46.wireOp",EDGE,"E76.left"),sQuery(id+"F46.wireOp",EDGE,"E76.right"),sQuery(id+"F46.wireOp",EDGE,"E77.0")])],"isStart":true});
            var sketch = newSketch(context, id + "F50", { "sketchPlane" : qUnion([Q0])});
            skLineSegment(sketch, "E82.0.0", {"start": v(-304.8, 46.36) * mm, "end": v(152.4, 46.36) * mm});
            skLineSegment(sketch, "E82.0.2", {"start": v(152.4, 46.36) * mm, "end": v(-304.8, 46.36) * mm});
            skLineSegment(sketch, "E83.0.0", {"start": v(149.22, 43.18) * mm, "end": v(149.22, 43.18) * mm});
            skLineSegment(sketch, "E83.0.1", {"start": v(149.22, 43.18) * mm, "end": v(-304.8, 43.18) * mm});
            skLineSegment(sketch, "E83.0.2", {"start": v(-304.8, 43.18) * mm, "end": v(-304.8, 46.36) * mm});
            skLineSegment(sketch, "E83.0.4", {"start": v(152.4, 46.36) * mm, "end": v(152.4, 46.36) * mm});
            skLineSegment(sketch, "E84.bottom", {"start": v(152.4, 46.36) * mm, "end": v(149.22, 46.36) * mm});
            skLineSegment(sketch, "E84.top", {"start": v(152.4, 0) * mm, "end": v(149.22, 0) * mm});
            skLineSegment(sketch, "E84.left", {"start": v(152.4, 46.36) * mm, "end": v(152.4, 0) * mm});
            skLineSegment(sketch, "E84.right", {"start": v(149.22, 46.36) * mm, "end": v(149.22, 0) * mm});
            skSolve(sketch);
        }
        {
            var Q0;
            Q0 = qSketchRegion(id + "F50", true);
            extrude(context, id + "F51", {"entities" : qUnion([Q0]), "operationType" : NewBodyOperationType.ADD, "depth" : 658.8 * mm, "offsetDistance" : 25.4 * mm});
        }
        {
            var Q0;
            Q0=makeQuery(id+"F3.boolean.opBoolean","MERGE",FACE,{"derivedFrom":[makeQuery(id+"F1.opExtrude","SWEPT_FACE",FACE,{"disambiguationData":[OSD([sQuery(id+"F0.wireOp",EDGE,"E0.right")])]}),makeQuery(id+"F3.opExtrude","SWEPT_FACE",FACE,{"disambiguationData":[OSD([sQuery(id+"F2.wireOp",EDGE,"E1.left")])]})]});
            var sketch = newSketch(context, id + "F52", { "sketchPlane" : qUnion([Q0])});
            skLineSegment(sketch, "E85.0", {"start": v(-304.8, 46.36) * mm, "end": v(152.4, 46.36) * mm});
            skLineSegment(sketch, "E86.0", {"start": v(-914.4, 0) * mm, "end": v(914.4, 0) * mm});
            skLineSegment(sketch, "E87", {"start": v(152.4, 46.36) * mm, "end": v(152.4, 0) * mm});
            skLineSegment(sketch, "E88", {"start": v(-304.8, 46.36) * mm, "end": v(-304.8, 0) * mm});
            skSolve(sketch);
        }
        {
            var Q0;
            Q0 = qSketchRegion(id + "F52", true);
            extrude(context, id + "F53", {"entities" : qUnion([Q0]), "operationType" : NewBodyOperationType.ADD, "oppositeDirection" : true, "depth" : 3.17 * mm, "offsetDistance" : 25.4 * mm});
        }
        {
            var Q0;
            Q0=makeQuery(id+"F3.boolean.opBoolean","MERGE",FACE,{"derivedFrom":[makeQuery(id+"F1.opExtrude","SWEPT_FACE",FACE,{"disambiguationData":[OSD([sQuery(id+"F0.wireOp",EDGE,"E0.left")])]}),makeQuery(id+"F3.opExtrude","SWEPT_FACE",FACE,{"disambiguationData":[OSD([sQuery(id+"F2.wireOp",EDGE,"E1.right")])]})]});
            var sketch = newSketch(context, id + "F54", { "sketchPlane" : qUnion([Q0])});
            skLineSegment(sketch, "E89.0", {"start": v(-152.4, 46.36) * mm, "end": v(304.8, 46.36) * mm});
            skLineSegment(sketch, "E90.0", {"start": v(914.4, 0) * mm, "end": v(-914.4, 0) * mm});
            skLineSegment(sketch, "E91", {"start": v(-152.4, 46.36) * mm, "end": v(-152.4, 0) * mm});
            skLineSegment(sketch, "E92", {"start": v(304.8, 46.36) * mm, "end": v(304.8, 0) * mm});
            skSolve(sketch);
        }
        {
            var Q0;
            Q0 = qSketchRegion(id + "F54", true);
            extrude(context, id + "F55", {"entities" : qUnion([Q0]), "operationType" : NewBodyOperationType.ADD, "oppositeDirection" : true, "depth" : 3.17 * mm, "offsetDistance" : 25.4 * mm});
        }
        {
            var Q0;
            Q0=makeQuery(id+"F55.boolean.opBoolean","MERGE",FACE,{"derivedFrom":[makeQuery(id+"F53.boolean.opBoolean","MERGE",FACE,{"derivedFrom":[makeQuery(id+"F51.boolean.opBoolean","MERGE",FACE,{"derivedFrom":[makeQuery(id+"F49.boolean.opBoolean","MERGE",FACE,{"derivedFrom":[makeQuery(id+"F47.opExtrude","SWEPT_FACE",FACE,{"disambiguationData":[OSD([sQuery(id+"F46.wireOp",EDGE,"E76.right")])]}),makeQuery(id+"F49.opExtrude","SWEPT_FACE",FACE,{"disambiguationData":[OSD([sQuery(id+"F48.wireOp",EDGE,"E80.right")])]})]}),makeQuery(id+"F51.opExtrude","SWEPT_FACE",FACE,{"disambiguationData":[OSD([sQuery(id+"F50.wireOp",EDGE,"E83.0.2")])]})]}),makeQuery(id+"F53.opExtrude","SWEPT_FACE",FACE,{"disambiguationData":[OSD([sQuery(id+"F52.wireOp",EDGE,"E88")])]})]}),makeQuery(id+"F55.opExtrude","SWEPT_FACE",FACE,{"disambiguationData":[OSD([sQuery(id+"F54.wireOp",EDGE,"E92")])]})]});
            var sketch = newSketch(context, id + "F56", { "sketchPlane" : qUnion([Q0])});
            skLineSegment(sketch, "E93.0", {"start": v(-660.4, 46.35) * mm, "end": v(-1.59, 46.35) * mm});
            skLineSegment(sketch, "E93.1", {"start": v(-660.4, 0) * mm, "end": v(-660.4, 46.35) * mm});
            skLineSegment(sketch, "E93.2", {"start": v(-660.4, 0) * mm, "end": v(660.4, 0) * mm});
            skLineSegment(sketch, "E93.3", {"start": v(660.4, 46.35) * mm, "end": v(1.59, 46.35) * mm});
            skLineSegment(sketch, "E93.4", {"start": v(660.4, 0) * mm, "end": v(660.4, 46.35) * mm});
            skLineSegment(sketch, "E94", {"start": v(-1.59, 46.35) * mm, "end": v(1.59, 46.35) * mm});
            skSolve(sketch);
        }
        {
            var Q0;
            Q0 = qSketchRegion(id + "F56", true);
            extrude(context, id + "F57", {"entities" : qUnion([Q0]), "operationType" : NewBodyOperationType.ADD, "oppositeDirection" : true, "depth" : 3.17 * mm, "offsetDistance" : 25.4 * mm});
        }
        {
            var Q0;
            Q0=makeQuery(id+"F51.opExtrude","SWEPT_FACE",FACE,{"disambiguationData":[OSD([sQuery(id+"F50.wireOp",EDGE,"E82.0.0")])]});
            cPlane(context, id + "F58", {"entities" : qUnion([Q0]), "cplaneType" : CPlaneType.OFFSET, "offset" : 457.2 * mm, "width" : 152.4 * mm, "height" : 152.4 * mm});
        }
        {
            var Q0;
            Q0=qCreatedBy(id+"F58.planeOp",FACE);
            var sketch = newSketch(context, id + "F59", { "sketchPlane" : qUnion([Q0])});
            skPoint(sketch, "E95.0", {"position": v(-609.6, 304.8) * mm});
            skPoint(sketch, "E96", {"position": v(-611.19, -152.4) * mm});
            skLineSegment(sketch, "E97.bottom", {"start": v(-611.19, -152.4) * mm, "end": v(-1.59, -152.4) * mm});
            skLineSegment(sketch, "E97.top", {"start": v(-611.19, 304.8) * mm, "end": v(-1.59, 304.8) * mm});
            skLineSegment(sketch, "E97.left", {"start": v(-611.19, -152.4) * mm, "end": v(-611.19, 304.8) * mm});
            skLineSegment(sketch, "E97.right", {"start": v(-1.59, -152.4) * mm, "end": v(-1.59, 304.8) * mm});
            skPoint(sketch, "E98.1", {"position": v(-1.59, -152.4) * mm});
            skSolve(sketch);
        }
        {
            var Q0;
            Q0 = qSketchRegion(id + "F59", true);
            extrude(context, id + "F60", {"entities" : qUnion([Q0]), "depth" : 254 * mm, "offsetDistance" : 25.4 * mm});
        }
        {
            var Q0;
            Q0=makeQuery(id+"F60.opExtrude","CAP_FACE",FACE,{"disambiguationData":[OSD([sQuery(id+"F59.wireOp",EDGE,"E97.bottom"),sQuery(id+"F59.wireOp",EDGE,"E97.top"),sQuery(id+"F59.wireOp",EDGE,"E97.left"),sQuery(id+"F59.wireOp",EDGE,"E97.right")])],"isStart":false});
            var sketch = newSketch(context, id + "F61", { "sketchPlane" : qUnion([Q0])});
            skLineSegment(sketch, "E99.0", {"start": v(-20.64, 292.1) * mm, "end": v(-592.14, 292.1) * mm});
            skLineSegment(sketch, "E99.1", {"start": v(-14.29, -133.35) * mm, "end": v(-14.29, 285.75) * mm});
            skLineSegment(sketch, "E99.2", {"start": v(-592.14, -139.7) * mm, "end": v(-20.64, -139.7) * mm});
            skLineSegment(sketch, "E99.3", {"start": v(-598.49, 285.75) * mm, "end": v(-598.49, -133.35) * mm});
            skPoint(sketch, "E100.visualSharp", {"position": v(-598.49, 292.1) * mm});
            skArc(sketch, "E100.filletArc", {"start": v(-592.14, 292.1) * mm, "mid": v(-596.63, 290.24) * mm, "end": v(-598.49, 285.75) * mm});
            skPoint(sketch, "E101.visualSharp", {"position": v(-14.29, 292.1) * mm});
            skArc(sketch, "E101.filletArc", {"start": v(-14.29, 285.75) * mm, "mid": v(-16.15, 290.24) * mm, "end": v(-20.64, 292.1) * mm});
            skPoint(sketch, "E102.visualSharp", {"position": v(-14.29, -139.7) * mm});
            skArc(sketch, "E102.filletArc", {"start": v(-20.64, -139.7) * mm, "mid": v(-16.15, -137.84) * mm, "end": v(-14.29, -133.35) * mm});
            skPoint(sketch, "E103.visualSharp", {"position": v(-598.49, -139.7) * mm});
            skArc(sketch, "E103.filletArc", {"start": v(-598.49, -133.35) * mm, "mid": v(-596.63, -137.84) * mm, "end": v(-592.14, -139.7) * mm});
            skSolve(sketch);
        }
        {
            var Q0;
            Q0 = qSketchRegion(id + "F61", true);
            extrude(context, id + "F62", {"entities" : qUnion([Q0]), "operationType" : NewBodyOperationType.REMOVE, "oppositeDirection" : true, "depth" : 241.3 * mm, "offsetDistance" : 25.4 * mm});
        }
        {
            var Q0;
            Q0=makeQuery(id+"F60.opExtrude","SWEPT_FACE",FACE,{"disambiguationData":[OSD([sQuery(id+"F59.wireOp",EDGE,"E97.bottom")])]});
            var sketch = newSketch(context, id + "F63", { "sketchPlane" : qUnion([Q0])});
            skLineSegment(sketch, "E104.bottom", {"start": v(-611.19, 503.56) * mm, "end": v(-598.49, 503.56) * mm});
            skLineSegment(sketch, "E104.top", {"start": v(-611.19, 757.56) * mm, "end": v(-598.49, 757.56) * mm});
            skLineSegment(sketch, "E104.left", {"start": v(-611.19, 503.56) * mm, "end": v(-611.19, 757.56) * mm});
            skLineSegment(sketch, "E104.right", {"start": v(-598.49, 503.56) * mm, "end": v(-598.49, 757.56) * mm});
            skLineSegment(sketch, "E105", {"start": v(-534.99, 757.56) * mm, "end": v(-611.19, 681.36) * mm});
            skLineSegment(sketch, "E106", {"start": v(-534.99, 757.56) * mm, "end": v(-611.19, 757.56) * mm});
            skSolve(sketch);
        }
        {
            var Q0;
            Q0 = qSketchRegion(id + "F63", true);
            extrude(context, id + "F64", {"entities" : qUnion([Q0]), "operationType" : NewBodyOperationType.REMOVE, "endBound" : BoundingType.THROUGH_ALL, "oppositeDirection" : true, "depth" : 25.4 * mm, "offsetDistance" : 25.4 * mm});
        }
        {
            var Q0;
            Q0=makeQuery(id+"F64.boolean.opBoolean","COPY",FACE,{"derivedFrom":makeQuery(id+"F64.opExtrude","SWEPT_FACE",FACE,{"disambiguationData":[OSD([sQuery(id+"F63.wireOp",EDGE,"E104.right")])]})});
            var sketch = newSketch(context, id + "F65", { "sketchPlane" : qUnion([Q0])});
            skLineSegment(sketch, "E107.0", {"start": v(139.7, 516.26) * mm, "end": v(139.7, 700.4) * mm});
            skLineSegment(sketch, "E107.1", {"start": v(-292.1, 516.26) * mm, "end": v(-292.1, 700.4) * mm});
            skLineSegment(sketch, "E107.2", {"start": v(133.35, 516.26) * mm, "end": v(-285.75, 516.26) * mm});
            skLineSegment(sketch, "E108", {"start": v(-285.75, 516.26) * mm, "end": v(-292.1, 516.26) * mm});
            skLineSegment(sketch, "E109", {"start": v(139.7, 516.26) * mm, "end": v(133.35, 516.26) * mm});
            skLineSegment(sketch, "E110", {"start": v(139.7, 700.4) * mm, "end": v(-292.1, 700.4) * mm});
            skSolve(sketch);
        }
        {
            var Q0;
            Q0 = qSketchRegion(id + "F65", true);
            extrude(context, id + "F66", {"entities" : qUnion([Q0]), "operationType" : NewBodyOperationType.REMOVE, "oppositeDirection" : true, "depth" : 25.4 * mm, "offsetDistance" : 25.4 * mm});
        }
        {
            var Q0;
            Q0=makeQuery(id+"F66.boolean.opBoolean","MERGE",EDGE,{"derivedFrom":[makeQuery(id+"F62.boolean.opBoolean","COPY",EDGE,{"derivedFrom":makeQuery(id+"F62.opExtrude","CAP_EDGE",EDGE,{"disambiguationData":[OSD([sQuery(id+"F61.wireOp",EDGE,"E99.0")])],"isStart":false})}),makeQuery(id+"F66.opExtrude","SWEPT_EDGE",EDGE,{"disambiguationData":[OSD([sQuery(id+"F65.wireOp",EDGE,"E107.1"),sQuery(id+"F65.wireOp",EDGE,"E108")])]})]});
            var Q1;
            Q1=makeQuery(id+"F62.boolean.opBoolean","COPY",EDGE,{"derivedFrom":makeQuery(id+"F62.opExtrude","CAP_EDGE",EDGE,{"disambiguationData":[OSD([sQuery(id+"F61.wireOp",EDGE,"E99.1")])],"isStart":false})});
            fillet(context, id + "F67", {"entities" : qUnion([Q0, Q1]), "radius" : 25.4 * mm, "tangentPropagation" : true, "allowEdgeOverflow" : false});
        }
        {
            var Q0;
            Q0=makeQuery(id+"F64.boolean.opBoolean","COPY",FACE,{"derivedFrom":makeQuery(id+"F64.opExtrude","SWEPT_FACE",FACE,{"disambiguationData":[OSD([sQuery(id+"F63.wireOp",EDGE,"E104.right")])]})});
            var sketch = newSketch(context, id + "F68", { "sketchPlane" : qUnion([Q0])});
            skLineSegment(sketch, "E111.bottom", {"start": v(-304.8, 503.56) * mm, "end": v(152.4, 503.56) * mm});
            skLineSegment(sketch, "E111.top", {"start": v(-304.8, 694.06) * mm, "end": v(152.4, 694.06) * mm});
            skLineSegment(sketch, "E111.left", {"start": v(-304.8, 503.56) * mm, "end": v(-304.8, 694.06) * mm});
            skLineSegment(sketch, "E111.right", {"start": v(152.4, 503.56) * mm, "end": v(152.4, 694.06) * mm});
            skLineSegment(sketch, "E112.0", {"start": v(-292.1, 681.36) * mm, "end": v(139.7, 681.36) * mm});
            skLineSegment(sketch, "E112.1", {"start": v(-292.1, 516.26) * mm, "end": v(-292.1, 681.36) * mm});
            skLineSegment(sketch, "E112.2", {"start": v(-292.1, 516.26) * mm, "end": v(139.7, 516.26) * mm});
            skLineSegment(sketch, "E112.3", {"start": v(139.7, 516.26) * mm, "end": v(139.7, 681.36) * mm});
            skSolve(sketch);
        }
        {
            var Q0;
            Q0 = qSketchRegion(id + "F68", true);
            extrude(context, id + "F69", {"entities" : qUnion([Q0]), "depth" : 12.7 * mm, "offsetDistance" : 25.4 * mm});
        }
        {
            var Q0;
            Q0=makeQuery(id+"F69.opExtrude","CAP_FACE",FACE,{"disambiguationData":[OSD([sQuery(id+"F68.wireOp",EDGE,"E111.bottom"),sQuery(id+"F68.wireOp",EDGE,"E111.top"),sQuery(id+"F68.wireOp",EDGE,"E111.left"),sQuery(id+"F68.wireOp",EDGE,"E111.right"),sQuery(id+"F68.wireOp",EDGE,"E112.0"),sQuery(id+"F68.wireOp",EDGE,"E112.1"),sQuery(id+"F68.wireOp",EDGE,"E112.2"),sQuery(id+"F68.wireOp",EDGE,"E112.3")])],"isStart":false});
            var sketch = newSketch(context, id + "F70", { "sketchPlane" : qUnion([Q0])});
            skLineSegment(sketch, "E113.0", {"start": v(139.7, 516.26) * mm, "end": v(139.7, 681.36) * mm});
            skLineSegment(sketch, "E113.1", {"start": v(-292.1, 681.36) * mm, "end": v(139.7, 681.36) * mm});
            skLineSegment(sketch, "E113.2", {"start": v(-292.1, 516.26) * mm, "end": v(139.7, 516.26) * mm});
            skLineSegment(sketch, "E113.3", {"start": v(-292.1, 516.26) * mm, "end": v(-292.1, 681.36) * mm});
            skSolve(sketch);
        }
        {
            var Q0;
            Q0 = qSketchRegion(id + "F70", true);
            extrude(context, id + "F71", {"entities" : qUnion([Q0]), "oppositeDirection" : true, "depth" : 12.7 * mm, "offsetDistance" : 25.4 * mm});
        }
        {
            var Q0;
            {var subQ0=sQuery(id+"F46.wireOp",EDGE,"E77.0");var subQ1=sQuery(id+"F46.wireOp",EDGE,"E76.left");var subQ2=sQuery(id+"F46.wireOp",EDGE,"E76.right");var subQ3=sQuery(id+"F46.wireOp",EDGE,"E76.top");Q0=makeQuery(id+"F51.boolean.opBoolean","SPLIT",FACE,{"disambiguationData":[TD([makeQuery(id+"F47.opExtrude","SWEPT_FACE",FACE,{"disambiguationData":[OSD([subQ3])]})])],"derivedFrom":makeQuery(id+"F47.opExtrude","CAP_FACE",FACE,{"disambiguationData":[OSD([sQuery(id+"F46.wireOp",EDGE,"E76.bottom"),subQ3,subQ1,subQ2,subQ0])],"isStart":true})});}
            var sketch = newSketch(context, id + "F72", { "sketchPlane" : qUnion([Q0])});
            skLineSegment(sketch, "E114.0", {"start": v(152.4, 757.56) * mm, "end": v(-304.8, 757.56) * mm});
            skLineSegment(sketch, "E115.bottom", {"start": v(-304.8, 757.56) * mm, "end": v(152.4, 757.56) * mm});
            skLineSegment(sketch, "E115.top", {"start": v(-304.8, 1066.43) * mm, "end": v(152.4, 1066.43) * mm});
            skLineSegment(sketch, "E115.left", {"start": v(-304.8, 757.56) * mm, "end": v(-304.8, 1066.43) * mm});
            skLineSegment(sketch, "E115.right", {"start": v(152.4, 757.56) * mm, "end": v(152.4, 1066.43) * mm});
            skSolve(sketch);
        }
        {
            var Q0;
            Q0=makeQuery(id+"F1.opExtrude","CAP_FACE",FACE,{"disambiguationData":[OSD([sQuery(id+"F0.wireOp",EDGE,"E0.bottom"),sQuery(id+"F0.wireOp",EDGE,"E0.top"),sQuery(id+"F0.wireOp",EDGE,"E0.left"),sQuery(id+"F0.wireOp",EDGE,"E0.right")])],"isStart":true});
            var sketch = newSketch(context, id + "F73", { "sketchPlane" : qUnion([Q0])});
            skLineSegment(sketch, "E116.bottom", {"start": v(-539.75, 946.15) * mm, "end": v(539.75, 946.15) * mm});
            skLineSegment(sketch, "E116.top", {"start": v(-539.75, 1352.55) * mm, "end": v(539.75, 1352.55) * mm});
            skLineSegment(sketch, "E116.left", {"start": v(-539.75, 946.15) * mm, "end": v(-539.75, 1352.55) * mm});
            skLineSegment(sketch, "E116.right", {"start": v(539.75, 946.15) * mm, "end": v(539.75, 1352.55) * mm});
            skLineSegment(sketch, "E117", {"start": v(0, 0) * mm, "end": v(0, 145.51) * mm, "construction": true});
            skSolve(sketch);
        }
        {
            var Q0;
            Q0 = qSketchRegion(id + "F73", true);
            extrude(context, id + "F74", {"entities" : qUnion([Q0]), "oppositeDirection" : true, "depth" : 12.7 * mm, "offsetDistance" : 25.4 * mm});
        }
        {
            var Q0;
            Q0=makeQuery(id+"F37.opExtrude","SWEPT_FACE",FACE,{"disambiguationData":[OSD([sQuery(id+"F36.wireOp",EDGE,"E58.right")])]});
            var sketch = newSketch(context, id + "F75", { "sketchPlane" : qUnion([Q0])});
            skLineSegment(sketch, "E118", {"start": v(0, -22.54) * mm, "end": v(0, 51.21) * mm, "construction": true});
            skPoint(sketch, "E118.endSnap0", {"position": v(0, 0) * mm});
            skLineSegment(sketch, "E119", {"start": v(654.05, 127) * mm, "end": v(660.4, 127) * mm});
            skLineSegment(sketch, "E120", {"start": v(660.4, 127) * mm, "end": v(660.4, 123.82) * mm});
            skLineSegment(sketch, "E121", {"start": v(660.4, 123.82) * mm, "end": v(658.81, 123.82) * mm});
            skLineSegment(sketch, "E122", {"start": v(658.81, 123.82) * mm, "end": v(658.81, 126.2) * mm});
            skLineSegment(sketch, "E123", {"start": v(658.81, 126.2) * mm, "end": v(657.23, 126.2) * mm});
            skLineSegment(sketch, "E124", {"start": v(657.23, 126.2) * mm, "end": v(657.23, 123.82) * mm});
            skLineSegment(sketch, "E125", {"start": v(657.23, 123.82) * mm, "end": v(655.64, 123.82) * mm});
            skLineSegment(sketch, "E126", {"start": v(655.64, 123.82) * mm, "end": v(655.64, 126.2) * mm});
            skLineSegment(sketch, "E127", {"start": v(655.64, 126.2) * mm, "end": v(654.05, 126.2) * mm});
            skLineSegment(sketch, "E128", {"start": v(654.05, 126.2) * mm, "end": v(654.05, 127) * mm});
            skLineSegment(sketch, "E129", {"start": v(654.05, 63.5) * mm, "end": v(665.87, 63.5) * mm, "construction": true});
            skLineSegment(sketch, "E130.MirrorCS", {"start": v(654.05, 0) * mm, "end": v(660.4, 0) * mm});
            skLineSegment(sketch, "E131.MirrorCS", {"start": v(654.05, 0.8) * mm, "end": v(654.05, 0) * mm});
            skLineSegment(sketch, "E132.MirrorCS", {"start": v(655.64, 0.8) * mm, "end": v(654.05, 0.8) * mm});
            skLineSegment(sketch, "E133.MirrorCS", {"start": v(655.64, 3.17) * mm, "end": v(655.64, 0.8) * mm});
            skLineSegment(sketch, "E134.MirrorCS", {"start": v(658.81, 0.8) * mm, "end": v(657.23, 0.8) * mm});
            skLineSegment(sketch, "E135.MirrorCS", {"start": v(660.4, 3.17) * mm, "end": v(658.81, 3.17) * mm});
            skLineSegment(sketch, "E136.MirrorCS", {"start": v(657.23, 3.17) * mm, "end": v(655.64, 3.17) * mm});
            skLineSegment(sketch, "E137.MirrorCS", {"start": v(657.23, 0.8) * mm, "end": v(657.23, 3.17) * mm});
            skLineSegment(sketch, "E138.MirrorCS", {"start": v(658.81, 3.17) * mm, "end": v(658.81, 0.8) * mm});
            skLineSegment(sketch, "E139.MirrorCS", {"start": v(660.4, 0) * mm, "end": v(660.4, 3.17) * mm});
            skLineSegment(sketch, "E140.MirrorCS", {"start": v(-658.81, 123.82) * mm, "end": v(-658.81, 126.2) * mm});
            skLineSegment(sketch, "E141.MirrorCS", {"start": v(-657.23, 126.2) * mm, "end": v(-657.23, 123.82) * mm});
            skLineSegment(sketch, "E142.MirrorCS", {"start": v(-655.64, 126.2) * mm, "end": v(-654.05, 126.2) * mm});
            skLineSegment(sketch, "E143.MirrorCS", {"start": v(-655.64, 123.82) * mm, "end": v(-655.64, 126.2) * mm});
            skLineSegment(sketch, "E144.MirrorCS", {"start": v(-658.81, 126.2) * mm, "end": v(-657.23, 126.2) * mm});
            skLineSegment(sketch, "E145.MirrorCS", {"start": v(-654.05, 126.2) * mm, "end": v(-654.05, 127) * mm});
            skLineSegment(sketch, "E146.MirrorCS", {"start": v(-654.05, 127) * mm, "end": v(-660.4, 127) * mm});
            skLineSegment(sketch, "E147.MirrorCS", {"start": v(-660.4, 127) * mm, "end": v(-660.4, 123.82) * mm});
            skLineSegment(sketch, "E148.MirrorCS", {"start": v(-657.23, 123.82) * mm, "end": v(-655.64, 123.82) * mm});
            skLineSegment(sketch, "E149.MirrorCS", {"start": v(-660.4, 123.82) * mm, "end": v(-658.81, 123.82) * mm});
            skLineSegment(sketch, "E150.MirrorCS", {"start": v(-657.23, 3.17) * mm, "end": v(-655.64, 3.17) * mm});
            skLineSegment(sketch, "E151.MirrorCS", {"start": v(-658.81, 0.8) * mm, "end": v(-657.23, 0.8) * mm});
            skLineSegment(sketch, "E152.MirrorCS", {"start": v(-654.05, 0.8) * mm, "end": v(-654.05, 0) * mm});
            skLineSegment(sketch, "E153.MirrorCS", {"start": v(-658.81, 3.17) * mm, "end": v(-658.81, 0.8) * mm});
            skLineSegment(sketch, "E154.MirrorCS", {"start": v(-655.64, 3.17) * mm, "end": v(-655.64, 0.8) * mm});
            skLineSegment(sketch, "E155.MirrorCS", {"start": v(-657.23, 0.8) * mm, "end": v(-657.23, 3.17) * mm});
            skLineSegment(sketch, "E156.MirrorCS", {"start": v(-655.64, 0.8) * mm, "end": v(-654.05, 0.8) * mm});
            skLineSegment(sketch, "E157.MirrorCS", {"start": v(-660.4, 0) * mm, "end": v(-660.4, 3.17) * mm});
            skLineSegment(sketch, "E158.MirrorCS", {"start": v(-654.05, 0) * mm, "end": v(-660.4, 0) * mm});
            skLineSegment(sketch, "E159.MirrorCS", {"start": v(-660.4, 3.17) * mm, "end": v(-658.81, 3.17) * mm});
            skLineSegment(sketch, "E160.MirrorCS", {"start": v(-654.05, 63.5) * mm, "end": v(-665.87, 63.5) * mm, "construction": true});
            skSolve(sketch);
        }
        {
            var Q0;
            Q0 = qSketchRegion(id + "F75", true);
            extrude(context, id + "F76", {"entities" : qUnion([Q0]), "operationType" : NewBodyOperationType.ADD, "oppositeDirection" : true, "depth" : 609.6 * mm, "offsetDistance" : 25.4 * mm});
        }
        {
            var Q0;
            Q0=makeQuery(id+"F76.boolean.opBoolean","MERGE",FACE,{"derivedFrom":[makeQuery(id+"F37.opExtrude","SWEPT_FACE",FACE,{"disambiguationData":[OSD([sQuery(id+"F36.wireOp",EDGE,"E58.right")])]}),makeQuery(id+"F76.opExtrude","CAP_FACE",FACE,{"disambiguationData":[OSD([sQuery(id+"F75.wireOp",EDGE,"E119"),sQuery(id+"F75.wireOp",EDGE,"E120"),sQuery(id+"F75.wireOp",EDGE,"E121"),sQuery(id+"F75.wireOp",EDGE,"E122"),sQuery(id+"F75.wireOp",EDGE,"E123"),sQuery(id+"F75.wireOp",EDGE,"E124"),sQuery(id+"F75.wireOp",EDGE,"E125"),sQuery(id+"F75.wireOp",EDGE,"E126"),sQuery(id+"F75.wireOp",EDGE,"E127"),sQuery(id+"F75.wireOp",EDGE,"E128")])],"isStart":true}),makeQuery(id+"F76.opExtrude","CAP_FACE",FACE,{"disambiguationData":[OSD([sQuery(id+"F75.wireOp",EDGE,"E130.MirrorCS"),sQuery(id+"F75.wireOp",EDGE,"E131.MirrorCS"),sQuery(id+"F75.wireOp",EDGE,"E132.MirrorCS"),sQuery(id+"F75.wireOp",EDGE,"E133.MirrorCS"),sQuery(id+"F75.wireOp",EDGE,"E134.MirrorCS"),sQuery(id+"F75.wireOp",EDGE,"E135.MirrorCS"),sQuery(id+"F75.wireOp",EDGE,"E136.MirrorCS"),sQuery(id+"F75.wireOp",EDGE,"E137.MirrorCS"),sQuery(id+"F75.wireOp",EDGE,"E138.MirrorCS"),sQuery(id+"F75.wireOp",EDGE,"E139.MirrorCS")])],"isStart":true}),makeQuery(id+"F76.opExtrude","CAP_FACE",FACE,{"disambiguationData":[OSD([sQuery(id+"F75.wireOp",EDGE,"E140.MirrorCS"),sQuery(id+"F75.wireOp",EDGE,"E141.MirrorCS"),sQuery(id+"F75.wireOp",EDGE,"E142.MirrorCS"),sQuery(id+"F75.wireOp",EDGE,"E143.MirrorCS"),sQuery(id+"F75.wireOp",EDGE,"E144.MirrorCS"),sQuery(id+"F75.wireOp",EDGE,"E145.MirrorCS"),sQuery(id+"F75.wireOp",EDGE,"E146.MirrorCS"),sQuery(id+"F75.wireOp",EDGE,"E147.MirrorCS"),sQuery(id+"F75.wireOp",EDGE,"E148.MirrorCS"),sQuery(id+"F75.wireOp",EDGE,"E149.MirrorCS")])],"isStart":true}),makeQuery(id+"F76.opExtrude","CAP_FACE",FACE,{"disambiguationData":[OSD([sQuery(id+"F75.wireOp",EDGE,"E150.MirrorCS"),sQuery(id+"F75.wireOp",EDGE,"E151.MirrorCS"),sQuery(id+"F75.wireOp",EDGE,"E152.MirrorCS"),sQuery(id+"F75.wireOp",EDGE,"E153.MirrorCS"),sQuery(id+"F75.wireOp",EDGE,"E154.MirrorCS"),sQuery(id+"F75.wireOp",EDGE,"E155.MirrorCS"),sQuery(id+"F75.wireOp",EDGE,"E156.MirrorCS"),sQuery(id+"F75.wireOp",EDGE,"E157.MirrorCS"),sQuery(id+"F75.wireOp",EDGE,"E158.MirrorCS"),sQuery(id+"F75.wireOp",EDGE,"E159.MirrorCS")])],"isStart":true})]});
            var sketch = newSketch(context, id + "F77", { "sketchPlane" : qUnion([Q0])});
            skLineSegment(sketch, "E161.bottom", {"start": v(654.3, 125.95) * mm, "end": v(655.38, 125.95) * mm});
            skLineSegment(sketch, "E161.top", {"start": v(654.3, 1.05) * mm, "end": v(655.38, 1.05) * mm});
            skLineSegment(sketch, "E161.left", {"start": v(654.3, 125.95) * mm, "end": v(654.3, 1.05) * mm});
            skLineSegment(sketch, "E161.right", {"start": v(655.38, 125.95) * mm, "end": v(655.38, 1.05) * mm});
            skLineSegment(sketch, "E162", {"start": v(656.43, 123.82) * mm, "end": v(656.43, 125.65) * mm, "construction": true});
            skLineSegment(sketch, "E163.MirrorCS", {"start": v(658.56, 1.05) * mm, "end": v(657.48, 1.05) * mm});
            skLineSegment(sketch, "E164.MirrorCS", {"start": v(658.56, 125.95) * mm, "end": v(657.48, 125.95) * mm});
            skLineSegment(sketch, "E165.MirrorCS", {"start": v(657.48, 125.95) * mm, "end": v(657.48, 1.05) * mm});
            skLineSegment(sketch, "E166.MirrorCS", {"start": v(658.56, 125.95) * mm, "end": v(658.56, 1.05) * mm});
            skLineSegment(sketch, "E167", {"start": v(0, 0) * mm, "end": v(0, 41.2) * mm, "construction": true});
            skLineSegment(sketch, "E168.MirrorCS", {"start": v(-658.56, 125.95) * mm, "end": v(-657.48, 125.95) * mm});
            skLineSegment(sketch, "E169.MirrorCS", {"start": v(-654.3, 125.95) * mm, "end": v(-655.38, 125.95) * mm});
            skLineSegment(sketch, "E170.MirrorCS", {"start": v(-654.3, 1.05) * mm, "end": v(-655.38, 1.05) * mm});
            skLineSegment(sketch, "E171.MirrorCS", {"start": v(-658.56, 1.05) * mm, "end": v(-657.48, 1.05) * mm});
            skLineSegment(sketch, "E172.MirrorCS", {"start": v(-656.43, 123.82) * mm, "end": v(-656.43, 125.65) * mm, "construction": true});
            skLineSegment(sketch, "E173.MirrorCS", {"start": v(-655.38, 125.95) * mm, "end": v(-655.38, 1.05) * mm});
            skLineSegment(sketch, "E174.MirrorCS", {"start": v(-654.3, 125.95) * mm, "end": v(-654.3, 1.05) * mm});
            skLineSegment(sketch, "E175.MirrorCS", {"start": v(-658.56, 125.95) * mm, "end": v(-658.56, 1.05) * mm});
            skLineSegment(sketch, "E176.MirrorCS", {"start": v(-657.48, 125.95) * mm, "end": v(-657.48, 1.05) * mm});
            skSolve(sketch);
        }
        {
            var Q0;
            Q0 = qSketchRegion(id + "F77", true);
            extrude(context, id + "F78", {"entities" : qUnion([Q0]), "oppositeDirection" : true, "depth" : 304.8 * mm, "offsetDistance" : 25.4 * mm});
        }
    });
